# Revit family: 515622930037
name_source: partatom
category: Plumbing Fixtures
revit_build: Autodesk Revit 2016 (Build: 20150220_1215(x64)
units: mm (PartAtom-declared; Revit-internal decimal feet)

## family parameters
Always vertical = Yes
Cut with Voids When Loaded = No
OmniClass Number = 23.45.55.00
OmniClass Title = Sanitary Faucets, Wastes
Part Type = Normal
Room Calculation Point = No
Round Connector Dimension = Use Diameter
Shared = No
Work Plane-Based = No

## types (1)
- 515622930037 Kitchen faucet
    Advanced Features = DZR brass
    Aerator = HONEYCOMB®
    AssetType = Fixed
    BIMObjectName = 515622930037
    BodyMaterial = Brass
    Brand = Hansa
    Category = Kitchen
    Class = Single lever, side operated
    CloseOffRating = 0
    Color = Chrome
    Connection Size = G1/2
    ConvergoRefNr = 0087-1803-0055-FI
    Customs Code = 84818011
    DN Size = DN15
    Description = Kitchen faucet with high swivel spout
    Dimension Drawing URL = http://static.hansa.com
    DurationUnit = Year
    EAN Number = 4057304004223
    FDV Document URL = http://www.hansa.com
    FaucetMainMaterial = Brass
    Features = Single lever, side operated
    Finish = Polished
    Flow = Limitation option for maximum flow-rate
    Flow Drawing URL = http://static.hansa.com
    Flow Rate At 300kPa = 0.2 L/s
    FlowCoefficient = 0
    Group = Kitchen faucets
    IfcExportAs = IfcValveType
    IfcExportType = FAUCET
    InletConnectionSize = 12 mm  [stored 0.0393701 ft]
    Installation Type = Deck mounted
    Installation and Maintenance = http://static.hansa.com
    Lever Handle = Lever with H+C symbol
    ManufacterURL = http://www.hansa.com
    Manufacturer = Hansa
    ManufacturerName = Hansa
    Market = AUS
    Material = Brass
    Max. Hot Water Supply = 80 °C
    Model = 515622930037 Kitchen faucet
    ModelReference = 515622930037
    Mounting Holes = 1 mounting hole
    NBSDescription = Water supply fittings for sinks
    NBSReference = 45-35-70/345
    Name = 515622930037 Kitchen faucet
    Name_en = 515622930037 Kitchen faucet
    Noise Class = I (ISO 3822) Oras lab.
    NominalDepth = 237 mm
    NominalHeight = 303 mm  [stored 0.994094 ft]
    NominalWidth = 103 mm
    Package Weight = 1.913 kg
    Package external Dimensions = 407 x 265 x 119
    Pipes = Flexible inlet pipe(s)
    Product Code = 515622930037
    Product Datasheet = http://www.hansa.com
    Product Family = HANSAPOLO
    Product Image URL = http://static.hansa.com
    Product URL = http://static.hansa.com
    ProductInformation = Kitchen faucet with high swivel spout
    Projection = 203 mm
    Shape = Sculptured
    Size = 103x237x303 mm
    Spare Parts = http://static.hansa.com
    Spout Swivel Range = 120° (60° / 0°)
    Spout Type = Swivel spout
    Temperature = Temperature limiter
    Uniclass2 = Pr_40_30_96_78
    Uniclass2015Description = Sink manual water supply sets
    Uniclass2015Reference = Pr_40_20_87_78
    Usage Group = Households
    Version = 1
    VersionDate = 15/03/2019
    WarrantyDescription = http://warranty.hansa.com
    WarrantyDurationUnit = Year
    WorkingPressure = 50 - 1000 kPa

note: [stored X ft] marks values corroborated as IEEE doubles in the binary element streams (Revit-internal decimal feet)

## geometry (parser evidence)
native form markers: Sweep x3
no freeform markers — native parametric forms only
